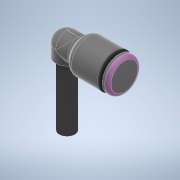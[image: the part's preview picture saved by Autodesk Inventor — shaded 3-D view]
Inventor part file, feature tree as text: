
AUTODESK INVENTOR PART (.ipt)
format: ipt  version: 2021 (Build 250183000, 183)  size: 200,704 bytes
history: native  units: mm
features: extrude x6, sketch x6, fillet x4, chamfer x1, projected_geometry x1
ambient origin geometry x8: Origin, YZ Plane, XZ Plane, XY Plane, X Axis, Y Axis, Z Axis, Center Point
bodies: Solid1 (feature_tree)
feature tree (18):
  extrude  "Extrusion1"  Depth=16.25mm TaperAngle=0.0deg
  extrude  "Extrusion2"  Depth=5.9mm TaperAngle=0.0deg
  extrude  "Extrusion3"  Depth=4.7mm TaperAngle=0.0deg
  extrude  "Extrusion4"  Depth=7.5mm TaperAngle=0.0deg
  extrude  "Extrusion5"  Depth=1.0mm TaperAngle=0.0deg
  extrude  "Extrusion6"  Depth=1.5mm TaperAngle=0.0deg
  fillet  "Fillet1"  Radius=0.8mm
  fillet  "Fillet2"  Radius=2.9mm
  chamfer  "Chamfer1"  Distance=1.2mm Angle=45.0deg
  fillet  "Fillet3"  Radius=1.5mm
  fillet  "Fillet4"  Radius=1.2mm
  sketch  "Sketch1"  dims[d0=4.0mm d1=16.25mm d2=0.0mm]
  sketch  "Sketch2"  dims[d3=5.9mm d4=5.9mm d5=0.0mm]
  sketch  "Sketch3"  dims[d6=5.9mm d7=4.7mm d8=0.0mm]
  projected_geometry  "Projected Loop1"
  sketch  "Sketch4"  dims[d9=8.8mm d10=7.5mm d11=0.0mm]
  sketch  "Sketch5"  dims[d12=5.0mm d13=1.0mm d14=0.0mm]
  sketch  "Sketch6"  dims[d15=8.5mm d16=1.5mm d17=0.0mm d18=0.8mm d19=2.9mm d20=1.2mm d21=2.0mm d22=45.0deg d23=1.5mm d24=1.2mm]
